# Revit family: HAR2430XXXX-Double
name_source: partatom
category: Furniture
units: mm (PartAtom-declared; Revit-internal decimal feet)

## family parameters
Always vertical = Yes
Cut with Voids When Loaded = No
OmniClass Number = 23.40.20.00
OmniClass Title = General Furniture and Specialties
Room Calculation Point = No
Shared = No
Work Plane-Based = No

## types (7) — shared parameters
C WT = Yes
FT 3CP = Yes
Low Emitting Finish = Yes
Low Emitting Material = Yes
Manufacturer = Palmer Hamilton
Product Documentation Link = https://palmerhamilton.com
Salvage or Reuse = Yes
Type Comments = Harmony
URL = https://palmerhamilton.com
zero-valued in all types: Cost, Percentage of Recycled Content

## per-type parameters (varying)
| type | Description | Front Panel L | Grommet L | Length | S WT | Width |
| HAR24304860 | Harmony, Double-Sided Table, 48WX60L | 53 1/4" | 15" | 60" | No | 48" |
| HAR24304872 | Harmony, Double-Sided Table, 48WX72L | 65 1/4" | 18" | 72" | No | 48" |
| HAR24304884 | Harmony, Double-Sided Table, 48WX84L | 77 1/4" | 14" | 84" | Yes | 48" |
| HAR24304896 | Harmony, Double-Sided Table, 48WX96L | 60" | 16" | 96" | Yes | 48" |
| HAR24306072 | Harmony, Double-Sided Table, 60WX72L | 65 1/4" | 18" | 72" | No | 60" |
| HAR24306084 | Harmony, Double-Sided Table, 60WX84L | 77 1/4" | 14" | 84" | Yes | 60" |
| HAR24306096 | Harmony, Double-Sided Table, 60WX96L | 89 1/4" | 16" | 96" | Yes | 60" |

note: column(s) folded — value = type name in every type: Model

## geometry (parser evidence)
native form markers: Sweep x67
no freeform markers — native parametric forms only
